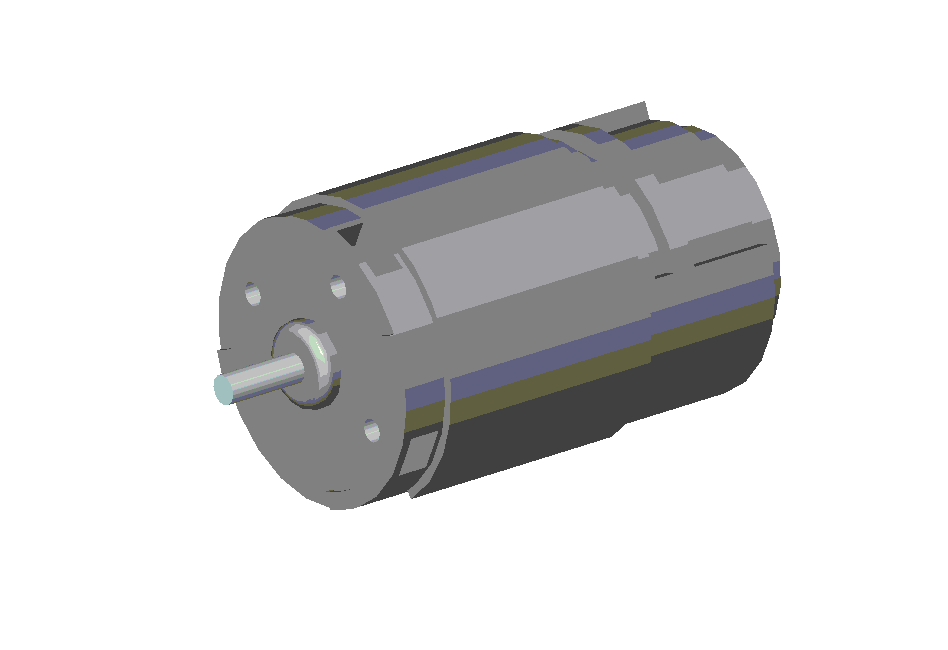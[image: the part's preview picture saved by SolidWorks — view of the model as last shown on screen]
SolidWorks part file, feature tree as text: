
SOLIDWORKS PART (.sldprt)
format: sldprt  version: not decoded by parser v0  size: 316,928 bytes
history: native  units: mm
features: sketch x11, cut_extrude x6, extrude x5, plane x4, pattern_circular x4, fillet x1 (+8 scaffold rows collapsed)
feature tree (39):
  scaffold x8  (default folders/planes/origin — collapsed)
  sketch  "Sketch1"  dims[D1=47.5mm]
  extrude  "Base-Extrude"  Depth=78.8mm
  plane  "Plane1"  Offset=7.78mm
  sketch  "Sketch2"  dims[D1=50.5mm]
  extrude  "Boss-Extrude1"  Depth=40mm
  sketch  "Sketch3"  dims[D1=14.6mm]
  extrude  "Boss-Extrude2"  Depth=3.5mm
  sketch  "Sketch4"  dims[D1=5.0mm]
  extrude  "Boss-Extrude3"  Depth=14.25mm
  sketch  "Sketch5"  dims[D1=4.0mm D2=16.4mm]
  cut_extrude  "Cut-Extrude2"  Depth=8mm
  pattern_circular  "CirPattern1"  Count=3 Angle=90deg
  fillet  "Fillet1"  Radius=2mm
  sketch  "Sketch6"  dims[c1.D1=~34.985446mm c2.D1=60.0deg c2.D2=~31.176664mm c3.D2=90.0deg c3.D1=~20.568103mm c3.D3=11.875mm c3.D4=1.5mm c3.D5=1.5mm]
  cut_extrude  "Cut-Extrude3"  [1 undecoded]
  sketch  "Sketch7"  dims[c1.D4=47.5mm c1.D5=41.5mm c1.D1=~31.582668mm c2.D1=45.0deg c2.D2=6.7mm c2.D3=3.35mm c3.D1=~12.111178mm c3.D3=~16.848794mm c3.D6=~3.034757mm]
  extrude  "Boss-Extrude4"  Depth=0.8mm
  pattern_circular  "CirPattern2"  Count=4 Angle=90deg
  plane  "Plane2"  Offset=1.45mm
  sketch  "Sketch8"  dims[c1.D5=~18.930773mm c1.D6=23.75mm c1.D1=4.0mm c1.D2=8.0mm c2.D1=4.0mm c2.D3=5.5mm c2.D4=11.0mm]
  cut_extrude  "Cut-Extrude4"  Depth=5.4mm
  pattern_circular  "CirPattern3"  Count=2 Angle=180deg
  sketch  "Sketch9"  dims[D1=37.0mm]
  cut_extrude  "Cut-Extrude5"  Depth=5.3mm
  plane  "Plane3"  Offset=50.75mm
  sketch  "Sketch10"  dims[D1=15.0mm D2=30.0mm]
  cut_extrude  "Cut-Extrude6"  Depth=4.2mm
  plane  "Plane4"  Offset=3.65mm
  sketch  "Sketch12"  dims[D1=3.0mm]
  cut_extrude  "Cut-Extrude9"  [1 undecoded]
  pattern_circular  "CirPattern4"  Count=2 Angle=180deg
decode coverage: 25 of 27 modeling features carry decoded parameters
note: ~ marks probable driven/reference dimensions
note: 2 parameter values undecoded
note: suppression state not decoded; provenance and decode notes live in map.json
